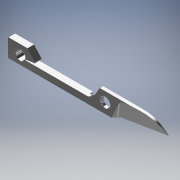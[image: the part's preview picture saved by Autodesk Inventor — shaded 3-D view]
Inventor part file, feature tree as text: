
AUTODESK INVENTOR PART (.ipt)
format: ipt  version: 2019 (Build 230136000, 136)  size: 246,272 bytes
history: native  units: mm (DEFAULTED — no unit token found)
features: sketch x7, fillet x7, extrude x5, other x2, plane x1, chamfer x1
ambient origin geometry x8: Origin, YZ Plane, XZ Plane, XY Plane, X Axis, Y Axis, Z Axis, Center Point
bodies: Solid1 (feature_tree)
feature tree (23):
  extrude  "Extrusion1"  Depth=50.0mm
  extrude  "Extrusion2"  Depth=3.0mm
  sketch  "Sketch4"  dims[d7=11.0mm d8=2.0mm]
  other  "Work Point2"
  other  "Work Point3"
  sketch  "Sketch8"  dims[d9=6.0mm d10=2.0mm d11=0.0mm d12=2.0mm d13=0.0mm d26=0.4mm d27=5.0mm d28=10.0mm d29=0.0mm d34=9.0mm d35=3.0mm]
  plane  "Work Plane6"
  extrude  "Extrusion5"  Depth=2.0mm
  extrude  "Extrusion6"  Depth=10.0mm TaperAngle=0.0deg
  fillet  "Fillet3"  Radius=2.0mm
  fillet  "Fillet5"  Radius=0.4mm
  fillet  "Fillet6"  Radius=5.0mm
  fillet  "Fillet8"  Radius=10.0mm
  fillet  "Fillet9"  Radius=9.0mm
  fillet  "Fillet10"  Radius=3.0mm
  extrude  "Extrusion8"  Depth=10.0mm
  fillet  "Fillet11"  Radius=10.0mm
  chamfer  "Chamfer3"  Distance=3.0mm
  sketch  "Sketch1"  dims[d3=2.9mm d4=50.0mm]
  sketch  "Sketch2"  dims[d5=29.5mm d6=3.0mm]
  sketch  "Sketch9"  dims[d36=3.8mm d37=2.6mm d38=10.0mm d39=0.0mm]
  sketch  "Sketch10"  dims[d40=0.2mm]
  sketch  "Sketch12"  dims[d42=0.2mm d43=3.0mm d44=20.5mm d45=120.0deg d46=4.0mm d50=3.0mm d52=75.0deg d54=45.0deg d56=0.25mm d57=1.0mm d58=0.25mm d59=15.0mm d60=0.5mm d61=23.5mm d62=15.5mm d63=1.6mm d64=6.5mm d65=10.0mm d66=0.0mm d67=0.2mm d68=0.1mm d69=0.1mm d70=45.0deg]
